# Revit family: WALL WASHER BUILDING RGBW_LV2610QW.10
name_source: partatom
category: Luminarias
units: mm (PartAtom-declared; Revit-internal decimal feet)

## family parameters
Compartido = No
Corte con vacíos al cargar = No
Cota de conector redondo = Diámetro de uso
Origen de luz = Sí
Punto de cálculo de habitación = No
Se basa en plano de trabajo = Sí
Siempre vertical = No
Tipo de pieza = Normal

## types (1)
- REFL_LV2610QW.10
    Archivo de red fotométrica = LV2610QW_FULL_10.IES
    Cambio de temperatura de color de luz atenuada = Curva de lámpara incandescente
    Comentarios de vataje = 90-277V
    Descripción = LUMINARIA TIPO REFLECTOR DIRIGIBLE, WALL WASHER, CUERPO DE ALUMINIO FUNDIDO A PRESION, 399MM DE DIAMETRO POR 195MM DE PROFUNDO CON UN PESO DE 14.6KG, CUENTA CON 26 LED TIPO CREE TECNOLOGIA RGBW CON UN CONSUMO TOTAL DE 290W, 9000 LUMENES FULL COLOUR, RGBW, IP 66, CABLE H07RN DE 1.5M, APERTURA DE 10 GRADOS POR PROYECTO, ALIMENTADA A 90-277V.
    Elevación por defecto = 0 mm  [stored 0 ft]
    Fabricante = BRILLANT
    Filtro de color = 16777215
    Lámpara = CREE
    Modelo = LV2610QW.10
    Watt per fixture = 290
    Ángulo de inclinación = 40.00°

note: [stored X ft] marks values corroborated as IEEE doubles in the binary element streams (Revit-internal decimal feet)

## geometry (parser evidence)
native form markers: Blend x2
no freeform markers — native parametric forms only
